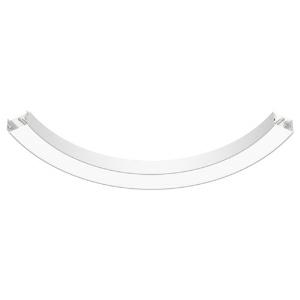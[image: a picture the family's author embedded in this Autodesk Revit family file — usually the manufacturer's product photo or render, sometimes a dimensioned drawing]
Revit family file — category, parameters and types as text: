
# Revit family: super-g_super-g__2100___120deg_hl_dir_indirekt_led__50_6w_7810lm_3000k_cri_80_430-1460_bc40
name_source: partatom
category: Leuchten
revit_build: Autodesk Revit 2016 (Build: 20190508_0715(x64)
units: mm (PartAtom-declared; Revit-internal decimal feet)

## family parameters
Basisbauteil = Fläche
Beim Laden mit Abzugskörper schneiden = Nein
Bemaßung runder Anschluss = Durchmesser verwenden
Gemeinsam genutzt = Nein
Lichtquelle = Nein
Raumberechnungspunkt = Nein
Teiletyp = Normal

## types (1)
- 430-1460- (1 x LED, 1115.7 lm, 3000K)
    Approval mark = CE
    Beschreibung = The insert consists of aluminum-extruded profile. Charming SOFT-EDGE design ensure unparalleled styling. The ballast is integrated and allows for an operation with 220-240V (50/60Hz). SUPER-G (# 430-1460) ist not dimmable (on/off).
    CIE Flux Codes = 48 80 96 58 70
    Color Rendering = 1B/80…89
    Color Temperature = 3000K
    Height = 120 mm
    Hersteller = Prolicht
    Lamp Light Flux = 1115.7 lm
    Lamp count = 1
    Lampe = 1 x LED
    Length = 314 mm
    Luminous efficacy = 98 lm/W
    ModVariant = Nein
    Modell = 430-1460
    Mounting Place = Ceiling
    Mounting Type = Pendant
    Number of Poles = 1
    OnlyDefault = Ja
    Power Factor = 1
    Product Name = SUPER-G__SUPER-G  2100 / 120° HL dir/indirekt LED: 50,6W 7810lm 3000K CRI:80
    Product group = Suspended profile systems
    ProductGroupID = 944
    Protection Class = Protection class I
    Protection Degree = IP 20
    RLX_Detail_Level = 1
    RlxData = <blob elided: 34393 chars, md5=9a76c298>
    Scheinlast = 56 VA
    Socket = socket
    Standby Power = 0 W
    System Light Flux = 5494 lm
    System Power = 56 W
    Typenbild = 430-1460.jpg
    URL = http://relux.com
    VarID = 430-1460-
    Voltage = 0 V
    Vorgabe-Ansicht = 1800 mm
    Weight = 0.00 kg
    Width = 150 mm

## geometry (parser evidence)
native form markers: Sweep x41
no freeform markers — native parametric forms only
